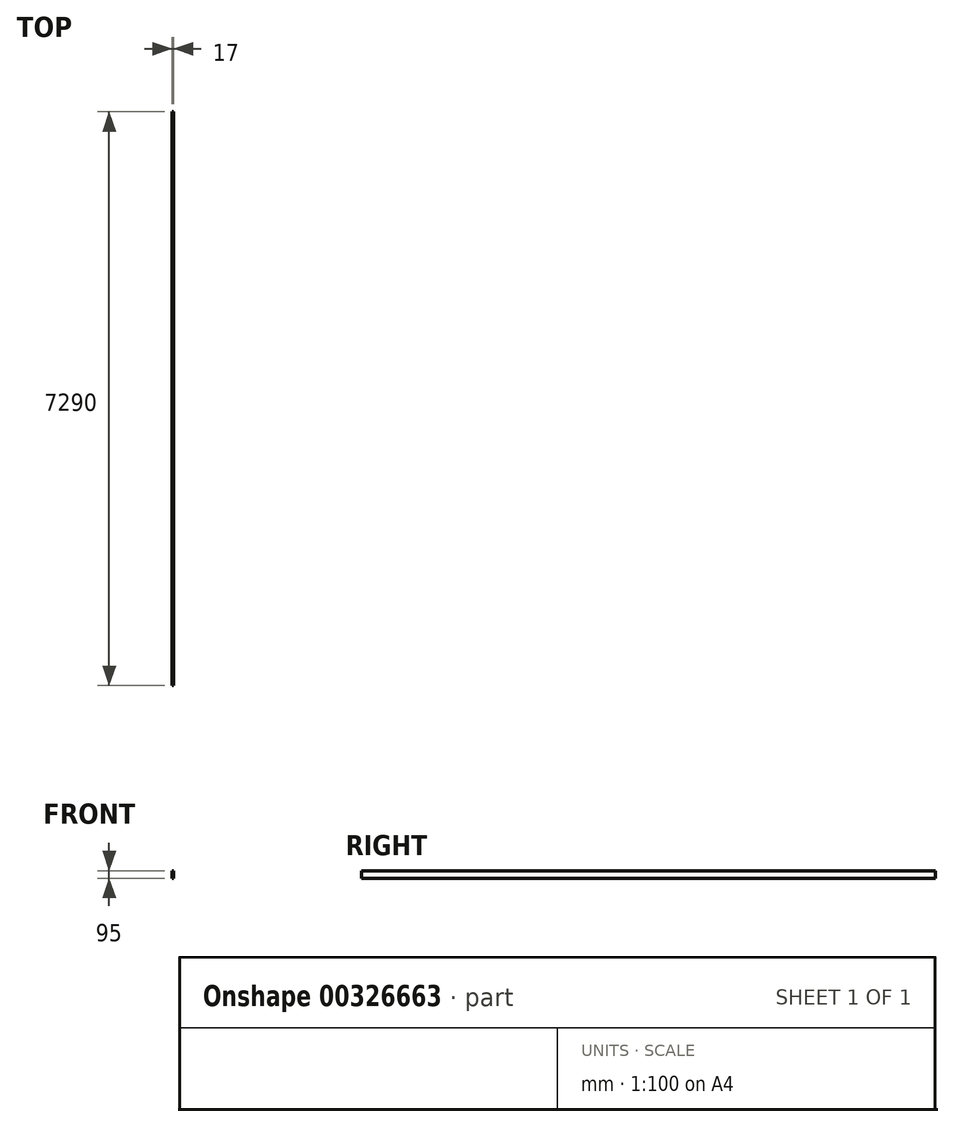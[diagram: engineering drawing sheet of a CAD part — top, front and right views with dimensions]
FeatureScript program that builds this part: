
annotation { "Feature Type Name" : "Feature", "Feature Type Description" : "" }
export const myFeature = defineFeature(function(context is Context, id is Id, definition is map)
    precondition{}
    {
        {
            var Q0;
            Q0=qCreatedBy(makeId("Front.planeOp"),FACE);
            var sketch = newSketch(context, id + "F0", { "sketchPlane" : qUnion([Q0])});
            skLineSegment(sketch, "E0.bottom", {"start": v(0, 0) * mm, "end": v(17, 0) * mm});
            skLineSegment(sketch, "E0.top", {"start": v(0, 95) * mm, "end": v(17, 95) * mm});
            skLineSegment(sketch, "E0.left", {"start": v(0, 0) * mm, "end": v(0, 95) * mm});
            skLineSegment(sketch, "E0.right", {"start": v(17, 0) * mm, "end": v(17, 95) * mm});
            skSolve(sketch);
        }
        {
            var Q0;
            Q0=makeQuery(id+"F0.imprint","IMPRINT",FACE,{"disambiguationData":[TD([[makeQuery(id+"F0.imprint","IMPRINT",EDGE,{"derivedFrom":sQuery(id+"F0.wireOp",EDGE,"E0.bottom")}),1.0]])]});
            extrude(context, id + "F1", {"entities" : qUnion([Q0]), "depth" : 7290 * mm});
        }
    });
